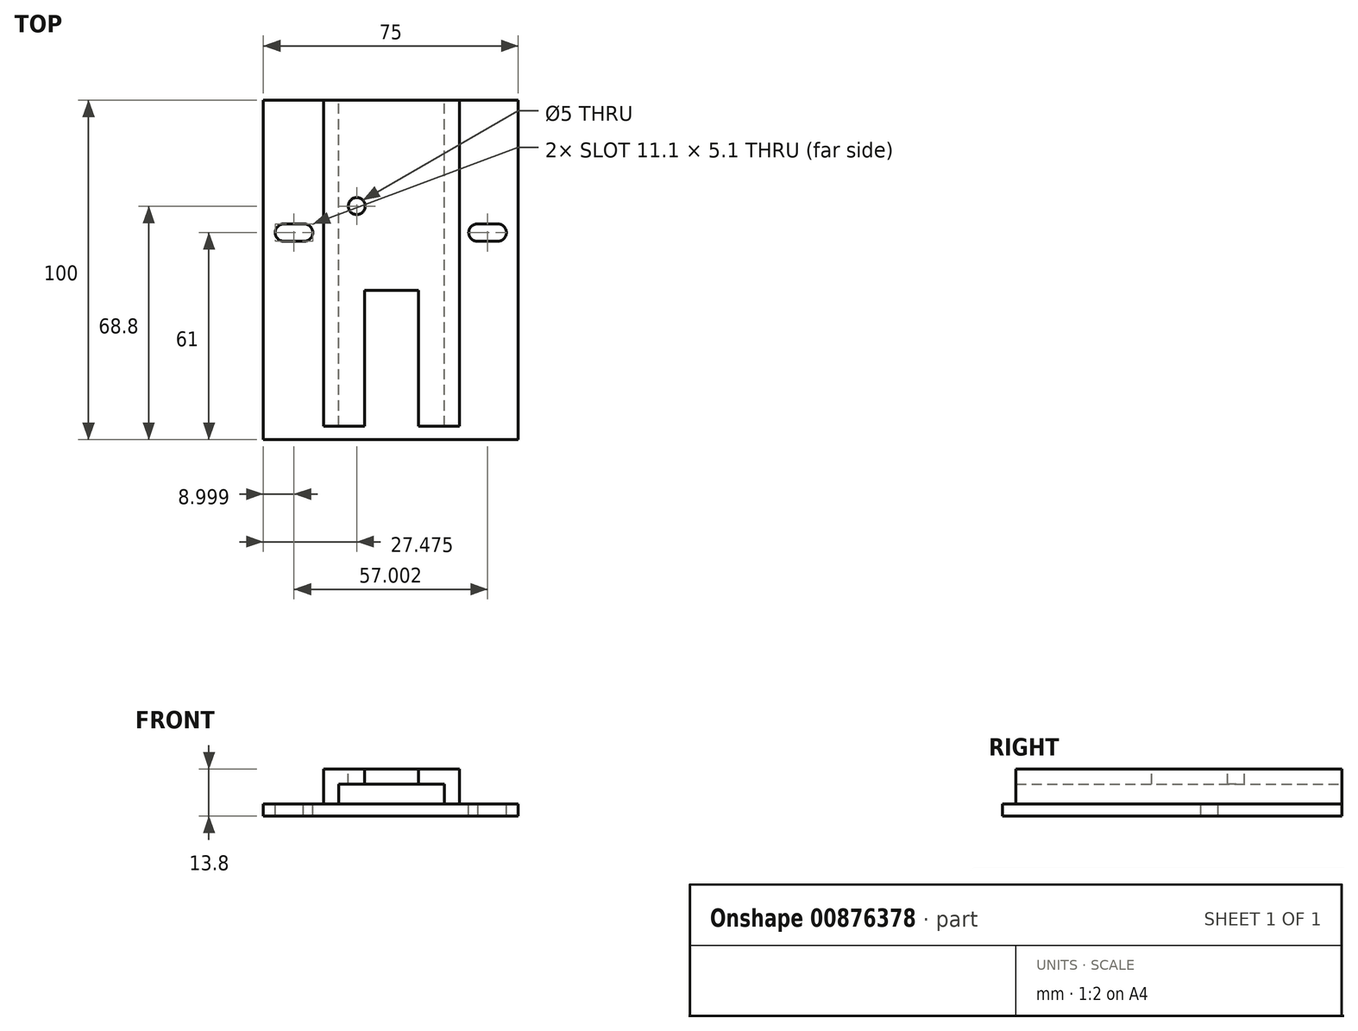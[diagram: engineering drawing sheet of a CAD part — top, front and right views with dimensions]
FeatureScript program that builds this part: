
annotation { "Feature Type Name" : "Feature", "Feature Type Description" : "" }
export const myFeature = defineFeature(function(context is Context, id is Id, definition is map)
    precondition{}
    {
        {
            var Q0;
            Q0=qCreatedBy(makeId("Top.planeOp"),FACE);
            var sketch = newSketch(context, id + "F0", { "sketchPlane" : qUnion([Q0])});
            skLineSegment(sketch, "E0.bottom", {"start": v(37.5, 50) * mm, "end": v(-37.5, 50) * mm});
            skLineSegment(sketch, "E0.top", {"start": v(37.5, -50) * mm, "end": v(-37.5, -50) * mm});
            skLineSegment(sketch, "E0.left", {"start": v(37.5, 50) * mm, "end": v(37.5, -50) * mm});
            skLineSegment(sketch, "E0.right", {"start": v(-37.5, 50) * mm, "end": v(-37.5, -50) * mm});
            skPoint(sketch, "E0.middle", {"position": v(0, 0) * mm});
            skSolve(sketch);
        }
        {
            var Q0;
            Q0 = qSketchRegion(id + "F0", true);
            extrude(context, id + "F1", {"entities" : qUnion([Q0]), "depth" : 3.5 * mm, "offsetDistance" : 25 * mm});
        }
        {
            var Q0;
            Q0=makeQuery(id+"F1.opExtrude","CAP_FACE",FACE,{"disambiguationData":[OSD([sQuery(id+"F0.wireOp",EDGE,"E0.bottom"),sQuery(id+"F0.wireOp",EDGE,"E0.top"),sQuery(id+"F0.wireOp",EDGE,"E0.left"),sQuery(id+"F0.wireOp",EDGE,"E0.right")])],"isStart":false});
            var sketch = newSketch(context, id + "F2", { "sketchPlane" : qUnion([Q0])});
            skArc(sketch, "E1", {"start": v(31.5, 8.45) * mm, "mid": v(34.05, 11) * mm, "end": v(31.5, 13.55) * mm});
            skArc(sketch, "E2", {"start": v(25.7, 13.54) * mm, "mid": v(22.95, 11.1) * mm, "end": v(25.5, 8.45) * mm});
            skLineSegment(sketch, "E3", {"start": v(25.7, 13.54) * mm, "end": v(31.5, 13.55) * mm});
            skLineSegment(sketch, "E4", {"start": v(31.5, 8.45) * mm, "end": v(25.5, 8.45) * mm});
            skArc(sketch, "E5.MirrorCS", {"start": v(-25.7, 13.54) * mm, "mid": v(-22.95, 11.1) * mm, "end": v(-25.5, 8.45) * mm});
            skLineSegment(sketch, "E6.MirrorCS", {"start": v(-25.7, 13.54) * mm, "end": v(-31.5, 13.55) * mm});
            skArc(sketch, "E7.MirrorCS", {"start": v(-31.5, 8.45) * mm, "mid": v(-34.05, 11) * mm, "end": v(-31.5, 13.55) * mm});
            skLineSegment(sketch, "E8.MirrorCS", {"start": v(-31.5, 8.45) * mm, "end": v(-25.5, 8.45) * mm});
            skSolve(sketch);
        }
        {
            var Q0;
            Q0 = qSketchRegion(id + "F2", true);
            extrude(context, id + "F3", {"entities" : qUnion([Q0]), "operationType" : NewBodyOperationType.REMOVE, "endBound" : BoundingType.UP_TO_NEXT, "oppositeDirection" : true, "depth" : 25 * mm, "offsetDistance" : 25 * mm});
        }
        {
            var Q0;
            Q0=makeQuery(id+"F1.opExtrude","CAP_FACE",FACE,{"disambiguationData":[OSD([sQuery(id+"F0.wireOp",EDGE,"E0.bottom"),sQuery(id+"F0.wireOp",EDGE,"E0.top"),sQuery(id+"F0.wireOp",EDGE,"E0.left"),sQuery(id+"F0.wireOp",EDGE,"E0.right")])],"isStart":false});
            var sketch = newSketch(context, id + "F4", { "sketchPlane" : qUnion([Q0])});
            skLineSegment(sketch, "E9.bottom", {"start": v(-19.75, 34) * mm, "end": v(20.25, 34) * mm});
            skLineSegment(sketch, "E9.top", {"start": v(-19.75, -6) * mm, "end": v(20.25, -6) * mm});
            skLineSegment(sketch, "E9.left", {"start": v(-19.75, 34) * mm, "end": v(-19.75, -6) * mm});
            skLineSegment(sketch, "E9.right", {"start": v(20.25, 34) * mm, "end": v(20.25, -6) * mm});
            skSolve(sketch);
        }
        {
            var Q0;
            Q0=makeQuery(id+"F4.imprint","IMPRINT",FACE,{"disambiguationData":[TD([[makeQuery(id+"F4.imprint","IMPRINT",EDGE,{"derivedFrom":sQuery(id+"F4.wireOp",EDGE,"E9.bottom")}),-1.0]])]});
            extrude(context, id + "F5", {"entities" : qUnion([Q0]), "operationType" : NewBodyOperationType.ADD, "depth" : 10.3 * mm, "offsetDistance" : 25 * mm});
        }
        {
            var Q0;
            Q0=makeQuery(id+"F5.opExtrude","SWEPT_FACE",FACE,{"disambiguationData":[OSD([sQuery(id+"F4.wireOp",EDGE,"E9.top")])]});
            var sketch = newSketch(context, id + "F6", { "sketchPlane" : qUnion([Q0])});
            skLineSegment(sketch, "E10", {"start": v(-19.75, 13.8) * mm, "end": v(-19.75, 3.5) * mm});
            skLineSegment(sketch, "E11", {"start": v(-19.75, 3.5) * mm, "end": v(-15.3, 3.5) * mm});
            skLineSegment(sketch, "E12", {"start": v(-15.3, 3.5) * mm, "end": v(-15.3, 9.4) * mm});
            skLineSegment(sketch, "E13", {"start": v(-15.3, 9.4) * mm, "end": v(-7.71, 9.4) * mm});
            skLineSegment(sketch, "E14", {"start": v(-7.71, 9.4) * mm, "end": v(-7.71, 13.8) * mm});
            skLineSegment(sketch, "E15", {"start": v(-7.71, 13.8) * mm, "end": v(-19.75, 13.8) * mm});
            skLineSegment(sketch, "E16", {"start": v(20.25, 13.8) * mm, "end": v(20.25, 3.5) * mm});
            skLineSegment(sketch, "E17", {"start": v(20.25, 3.5) * mm, "end": v(15.8, 3.5) * mm});
            skLineSegment(sketch, "E18", {"start": v(15.8, 3.5) * mm, "end": v(15.8, 9.4) * mm});
            skLineSegment(sketch, "E19", {"start": v(15.8, 9.4) * mm, "end": v(8.2, 9.4) * mm});
            skLineSegment(sketch, "E20", {"start": v(8.2, 9.4) * mm, "end": v(8.2, 13.8) * mm});
            skLineSegment(sketch, "E21", {"start": v(8.2, 13.8) * mm, "end": v(20.25, 13.8) * mm});
            skSolve(sketch);
        }
        {
            var Q0;
            Q0 = qSketchRegion(id + "F6", true);
            extrude(context, id + "F7", {"entities" : qUnion([Q0]), "operationType" : NewBodyOperationType.ADD, "depth" : 40 * mm, "offsetDistance" : 25 * mm});
        }
        {
            var Q0;
            Q0=makeQuery(id+"F5.opExtrude","SWEPT_FACE",FACE,{"disambiguationData":[OSD([sQuery(id+"F4.wireOp",EDGE,"E9.top")])]});
            var sketch = newSketch(context, id + "F8", { "sketchPlane" : qUnion([Q0])});
            skLineSegment(sketch, "E22.bottom", {"start": v(-15.3, 3.5) * mm, "end": v(15.8, 3.5) * mm});
            skLineSegment(sketch, "E22.top", {"start": v(-15.3, 9.4) * mm, "end": v(15.8, 9.4) * mm});
            skLineSegment(sketch, "E22.left", {"start": v(-15.3, 3.5) * mm, "end": v(-15.3, 9.4) * mm});
            skLineSegment(sketch, "E22.right", {"start": v(15.8, 3.5) * mm, "end": v(15.8, 9.4) * mm});
            skSolve(sketch);
        }
        {
            var Q0;
            Q0=makeQuery(id+"F7.boolean.opBoolean","MERGE",FACE,{"derivedFrom":[makeQuery(id+"F5.opExtrude","CAP_FACE",FACE,{"disambiguationData":[OSD([sQuery(id+"F4.wireOp",EDGE,"E9.bottom"),sQuery(id+"F4.wireOp",EDGE,"E9.top"),sQuery(id+"F4.wireOp",EDGE,"E9.left"),sQuery(id+"F4.wireOp",EDGE,"E9.right")])],"isStart":false}),makeQuery(id+"F7.opExtrude","SWEPT_FACE",FACE,{"disambiguationData":[OSD([sQuery(id+"F6.wireOp",EDGE,"8qMta25v-6CVy-Iscn-wtaU-9NbpmCGlRNgq")])]}),makeQuery(id+"F7.opExtrude","SWEPT_FACE",FACE,{"disambiguationData":[OSD([sQuery(id+"F6.wireOp",EDGE,"402ad5af-1585-4db2-8550-4120622850ed0.MirrorCS")])]})]});
            var sketch = newSketch(context, id + "F9", { "sketchPlane" : qUnion([Q0])});
            skCircle(sketch, "E23", {"center": v(-10.03, 18.8) * mm, "radius": 2.5 * mm});
            skSolve(sketch);
        }
        {
            var Q0;
            Q0 = qSketchRegion(id + "F9", true);
            extrude(context, id + "F10", {"entities" : qUnion([Q0]), "operationType" : NewBodyOperationType.REMOVE, "oppositeDirection" : true, "depth" : 5.5 * mm, "offsetDistance" : 25 * mm});
        }
        {
            var Q0;
            Q0=makeQuery(id+"F5.opExtrude","SWEPT_FACE",FACE,{"disambiguationData":[OSD([sQuery(id+"F4.wireOp",EDGE,"E9.bottom")])]});
            var sketch = newSketch(context, id + "F11", { "sketchPlane" : qUnion([Q0])});
            skLineSegment(sketch, "E24.bottom", {"start": v(-20.25, 3.5) * mm, "end": v(19.75, 3.5) * mm});
            skLineSegment(sketch, "E24.top", {"start": v(-20.25, 13.8) * mm, "end": v(19.75, 13.8) * mm});
            skLineSegment(sketch, "E24.left", {"start": v(-20.25, 3.5) * mm, "end": v(-20.25, 13.8) * mm});
            skLineSegment(sketch, "E24.right", {"start": v(19.75, 3.5) * mm, "end": v(19.75, 13.8) * mm});
            skSolve(sketch);
        }
        {
            var Q0;
            Q0 = qSketchRegion(id + "F11", true);
            extrude(context, id + "F12", {"entities" : qUnion([Q0]), "operationType" : NewBodyOperationType.ADD, "depth" : 16 * mm, "offsetDistance" : 25 * mm});
        }
        {
            var Q0;
            Q0 = qSketchRegion(id + "F8", true);
            extrude(context, id + "F13", {"entities" : qUnion([Q0]), "operationType" : NewBodyOperationType.REMOVE, "endBound" : BoundingType.UP_TO_NEXT, "oppositeDirection" : true, "depth" : 30 * mm, "offsetDistance" : 25 * mm});
        }
    });
